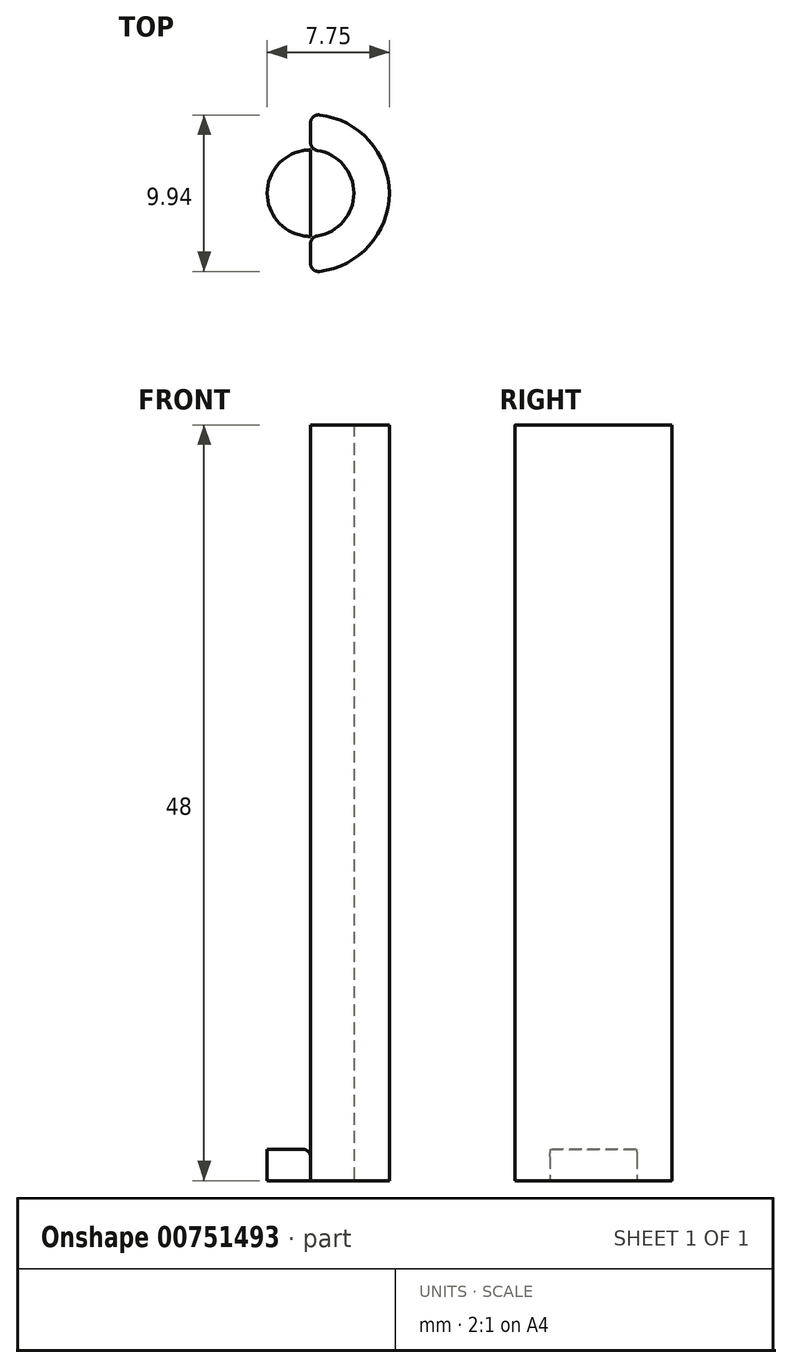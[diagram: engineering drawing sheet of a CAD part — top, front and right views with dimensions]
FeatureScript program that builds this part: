
annotation { "Feature Type Name" : "Feature", "Feature Type Description" : "" }
export const myFeature = defineFeature(function(context is Context, id is Id, definition is map)
    precondition{}
    {
        {
            var Q0;
            Q0=qCreatedBy(makeId("Top.planeOp"),FACE);
            var sketch = newSketch(context, id + "F0", { "sketchPlane" : qUnion([Q0])});
            skCircle(sketch, "E0", {"center": v(0, 0) * mm, "radius": 5 * mm});
            skCircle(sketch, "E1", {"center": v(0, 0) * mm, "radius": 2.75 * mm});
            skLineSegment(sketch, "E2", {"start": v(0, -5) * mm, "end": v(0, 5) * mm});
            skSolve(sketch);
        }
        {
            var Q0;
            {var subQ0=sQuery(id+"F0.wireOp",EDGE,"E2");var subQ1=sQuery(id+"F0.wireOp",EDGE,"E0");var subQ2=makeQuery(id+"F0.imprint","INTERSECT",VERTEX,{"disambiguationData":[OD(0.0)],"derivedFrom":[subQ1,subQ0]});Q0=makeQuery(id+"F0.imprint","IMPRINT",FACE,{"disambiguationData":[TD([[makeQuery(id+"F0.imprint","IMPRINT",EDGE,{"disambiguationData":[TD([[subQ2,1.0]])],"derivedFrom":subQ1}),1.0]])]});}
            extrude(context, id + "F1", {"entities" : qUnion([Q0]), "depth" : 48 * mm, "offsetDistance" : 25 * mm});
        }
        {
            var Q0;
            {var subQ0=sQuery(id+"F0.wireOp",EDGE,"E2");var subQ1=sQuery(id+"F0.wireOp",EDGE,"E1");var subQ2=makeQuery(id+"F0.imprint","INTERSECT",VERTEX,{"disambiguationData":[OD(0.0)],"derivedFrom":[subQ1,subQ0]});Q0=makeQuery(id+"F0.imprint","IMPRINT",FACE,{"disambiguationData":[TD([[makeQuery(id+"F0.imprint","IMPRINT",EDGE,{"disambiguationData":[TD([[subQ2,1.0]])],"derivedFrom":subQ1}),1.0]])]});}
            extrude(context, id + "F2", {"entities" : qUnion([Q0]), "operationType" : NewBodyOperationType.ADD, "depth" : 2 * mm, "offsetDistance" : 25 * mm});
        }
        {
            var Q0;
            {var subQ0=sQuery(id+"F0.wireOp",EDGE,"E2");var subQ1=sQuery(id+"F0.wireOp",EDGE,"E1");Q0=makeQuery(id+"F1.opExtrude","SWEPT_EDGE",EDGE,{"disambiguationData":[OSD([subQ1,subQ0]),TDD([makeQuery(id+"F0.imprint","INTERSECT",VERTEX,{"disambiguationData":[OD(0.0)],"derivedFrom":[subQ1,subQ0]})])]});}
            var Q1;
            {var subQ0=sQuery(id+"F0.wireOp",EDGE,"E2");var subQ1=sQuery(id+"F0.wireOp",EDGE,"E1");Q1=makeQuery(id+"F1.opExtrude","SWEPT_EDGE",EDGE,{"disambiguationData":[OSD([subQ1,subQ0]),TDD([makeQuery(id+"F0.imprint","INTERSECT",VERTEX,{"disambiguationData":[OD(1.0)],"derivedFrom":[subQ1,subQ0]})])]});}
            var Q2;
            {var subQ0=sQuery(id+"F0.wireOp",EDGE,"E2");var subQ1=sQuery(id+"F0.wireOp",EDGE,"E0");Q2=makeQuery(id+"F1.opExtrude","SWEPT_EDGE",EDGE,{"disambiguationData":[OSD([subQ1,subQ0]),TDD([makeQuery(id+"F0.imprint","INTERSECT",VERTEX,{"disambiguationData":[OD(0.0)],"derivedFrom":[subQ1,subQ0]})])]});}
            var Q3;
            {var subQ0=sQuery(id+"F0.wireOp",EDGE,"E2");var subQ1=sQuery(id+"F0.wireOp",EDGE,"E0");Q3=makeQuery(id+"F1.opExtrude","SWEPT_EDGE",EDGE,{"disambiguationData":[OSD([subQ1,subQ0]),TDD([makeQuery(id+"F0.imprint","INTERSECT",VERTEX,{"disambiguationData":[OD(1.0)],"derivedFrom":[subQ1,subQ0]})])]});}
            var Q4;
            Q4=makeQuery(id+"F2.opExtrude","CAP_EDGE",EDGE,{"disambiguationData":[OSD([sQuery(id+"F0.wireOp",EDGE,"E2")])],"isStart":false});
            fillet(context, id + "F3", {"entities" : qUnion([Q0, Q1, Q2, Q3, Q4]), "radius" : .5 * mm, "tangentPropagation" : true, "allowEdgeOverflow" : false});
        }
    });
